# Revit family: Скамейка опорная «Модерн»
name_source: partatom
category: Антураж
revit_build: Autodesk Revit 2017 (Build: 20160225_1515(x64)
units: mm (PartAtom-declared; Revit-internal decimal feet)

## family parameters
Всегда вертикально = Да
Источник визуального образа = Геометрия семейства
На основе рабочей плоскости = Нет
Общий = Нет
При загрузке вырезать с полостями = Нет
Точка расчета площади = Нет

## types (3) — shared parameters
ADSK_Код изделия = 11549
11549
ADSK_Материал доски = Ясень
ADSK_Материал опоры = Сталь, окрашенная, темно-серая, матовая
ADSK_Наименование = Скамейка опорная «Модерн»
ADSK_Размер_Ширина = 800 мм
URL = https://hobbyka.ru
Изготовитель = ООО "Хоббика"
zero-valued in all types: Высота

## per-type parameters (varying)
| type | ADSK_Размер_Длина | Длина доски | Стоимость |
| Скамейка опорная «Модерн» 1,2м | 1200 мм | 1130 мм | 4566 $ |
| Скамейка опорная «Модерн» 1,5м | 1500 мм | 1430 мм | 4954 $ |
| Скамейка опорная «Модерн» 1,8м | 1800 мм | 1730 мм | 5341 $ |
